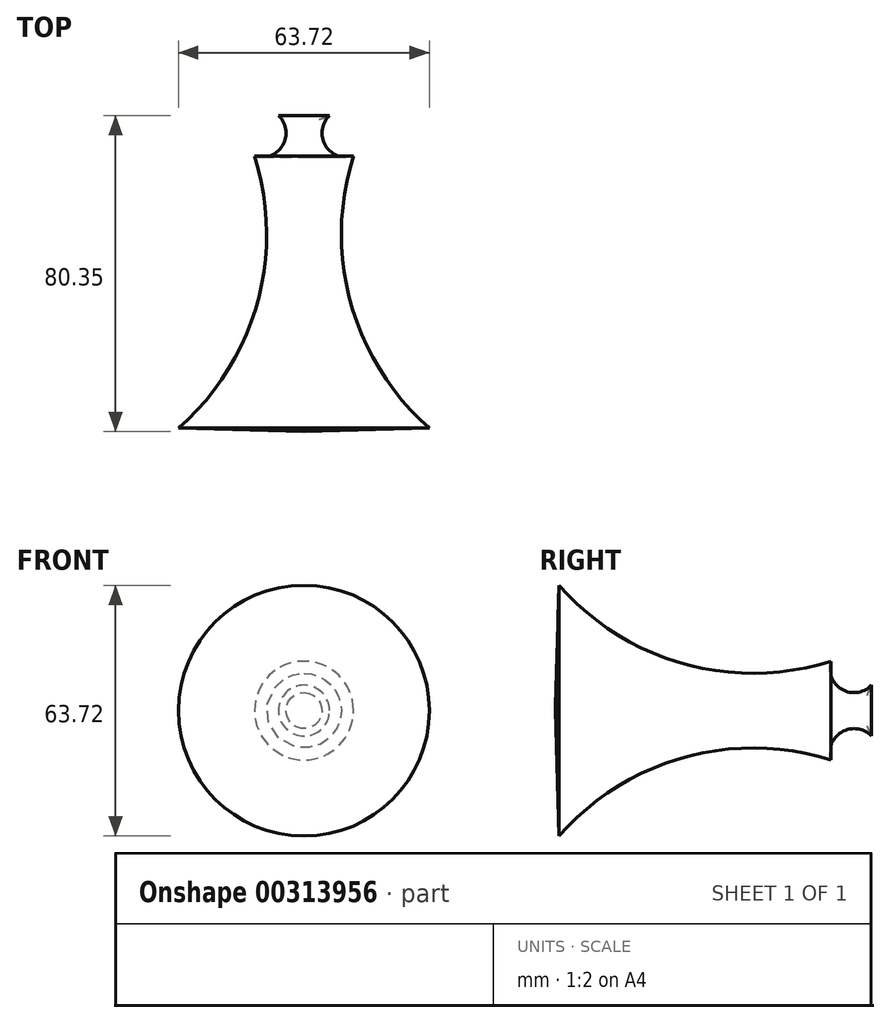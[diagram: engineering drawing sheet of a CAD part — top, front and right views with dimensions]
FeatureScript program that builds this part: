
annotation { "Feature Type Name" : "Feature", "Feature Type Description" : "" }
export const myFeature = defineFeature(function(context is Context, id is Id, definition is map)
    precondition{}
    {
        {
            var Q0;
            Q0=qCreatedBy(makeId("Top.planeOp"),FACE);
            var sketch = newSketch(context, id + "F0", { "sketchPlane" : qUnion([Q0])});
            skLineSegment(sketch, "E0", {"start": v(0, 46.52) * mm, "end": v(0, -52.33) * mm});
            skArc(sketch, "E1", {"start": v(0, 26.98) * mm, "mid": v(10.85, 35.7) * mm, "end": v(0, 44.42) * mm});
            skArc(sketch, "E2", {"start": v(6.47, 28.02) * mm, "mid": v(5.42, 20.44) * mm, "end": v(12.56, 17.68) * mm});
            skArc(sketch, "E3", {"start": v(12.56, 17.68) * mm, "mid": v(11.9, -19.74) * mm, "end": v(31.86, -51.4) * mm});
            skLineSegment(sketch, "E4", {"start": v(31.86, -51.4) * mm, "end": v(0, -52.33) * mm});
            skSolve(sketch);
        }
        {
            var Q0;
            {var subQ0=sQuery(id+"F0.wireOp",EDGE,"E2");Q0=makeQuery(id+"F0.imprint","IMPRINT",FACE,{"disambiguationData":[TD([[makeQuery(id+"F0.imprint","IMPRINT",EDGE,{"derivedFrom":subQ0}),-1.0]])]});}
            var Q1;
            {var subQ0=sQuery(id+"F0.wireOp",EDGE,"E1");var subQ1=sQuery(id+"F0.wireOp",EDGE,"E0");var subQ2=makeQuery(id+"F0.imprint","INTERSECT",VERTEX,{"disambiguationData":[OD(0.0)],"derivedFrom":[subQ1,subQ0]});Q1=makeQuery(id+"F0.imprint","IMPRINT",FACE,{"disambiguationData":[TD([[makeQuery(id+"F0.imprint","IMPRINT",EDGE,{"disambiguationData":[TD([[subQ2,1.0]])],"derivedFrom":subQ1}),1.0]])]});}
            var Q2;
            Q2=sQuery(id+"F0.wireOp",EDGE,"E0");
            revolve(context, id + "F1", {"entities" : qUnion([Q0, Q1]), "axis" : qUnion([Q2]), "revolveType" : RevolveType.FULL});
        }
    });
